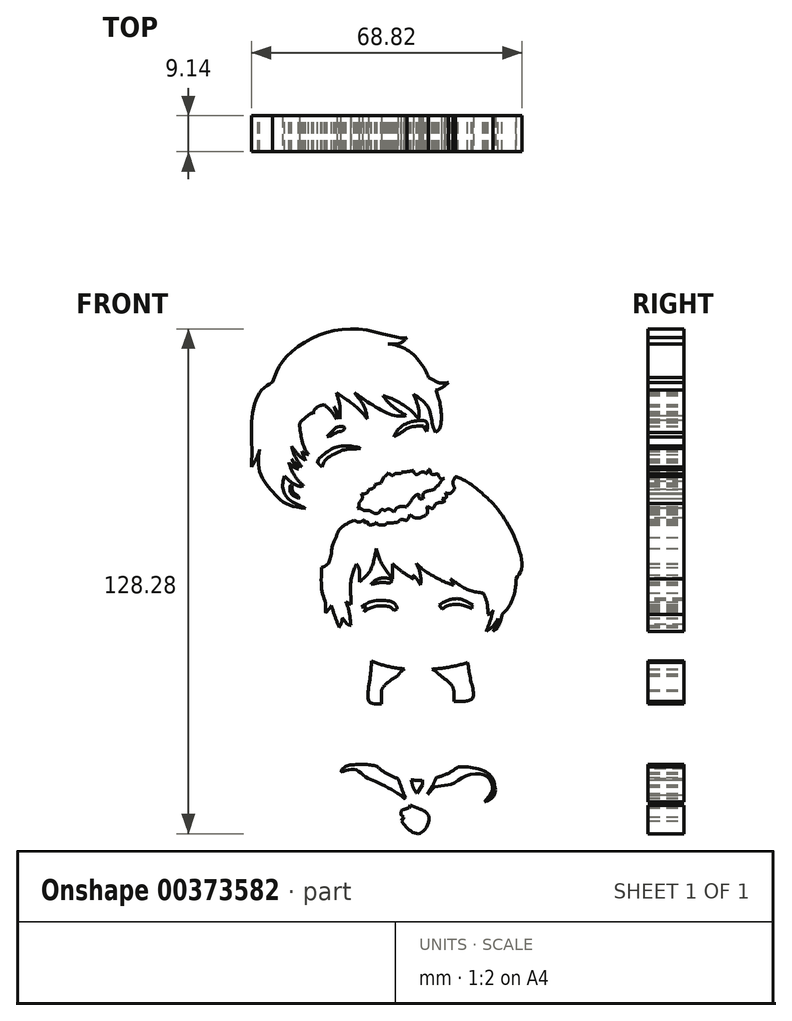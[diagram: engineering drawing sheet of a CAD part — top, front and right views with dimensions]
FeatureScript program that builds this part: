
annotation { "Feature Type Name" : "Feature", "Feature Type Description" : "" }
export const myFeature = defineFeature(function(context is Context, id is Id, definition is map)
    precondition{}
    {
        {
            var Q0;
            Q0=qCreatedBy(makeId("Front.planeOp"),FACE);
            var sketch = newSketch(context, id + "F0", { "sketchPlane" : qUnion([Q0])});
            skFitSpline(sketch, "E0", {"points": [v(-35.78, 54.46) * mm, v(-33.09, 59.85) * mm, v(-24.77, 66.06) * mm, v(-13.06, 67.81) * mm, v(-3.45, 65.7) * mm, v(-1.58, 65.82) * mm], "startDerivative": vector(10.86, 29.93) * mm, "endDerivative": vector(15.04, 3.36) * mm});
            skFitSpline(sketch, "E1", {"points": [v(-6.38, 64.18) * mm, v(-3.34, 64.3) * mm, v(-1.58, 65.82) * mm], "startDerivative": vector(6.22, -0.6) * mm, "endDerivative": vector(3.32, 3.98) * mm});
            skFitSpline(sketch, "E2", {"points": [v(-6.38, 64.18) * mm, v(-1.58, 62.66) * mm, v(2.4, 58.56) * mm, v(3.93, 55.63) * mm], "startDerivative": vector(14.2, -2.58) * mm, "endDerivative": vector(4.35, -9.84) * mm});
            skFitSpline(sketch, "E3", {"points": [v(3.93, 55.63) * mm, v(6.86, 54.23) * mm, v(8.96, 54.34) * mm], "startDerivative": vector(5.45, -3.31) * mm, "endDerivative": vector(4.6, 0.89) * mm});
            skFitSpline(sketch, "E4", {"points": [v(3.93, 54.21) * mm, v(5.68, 52.47) * mm, v(8.96, 54.34) * mm], "startDerivative": vector(3.48, -5.52) * mm, "endDerivative": vector(6.49, 5.4) * mm});
            skFitSpline(sketch, "E5", {"points": [v(5.68, 52.47) * mm, v(6.86, 48.72) * mm, v(6.86, 43.1) * mm, v(5.68, 41.7) * mm], "startDerivative": vector(3.82, -9.5) * mm, "endDerivative": vector(-5.74, -4.27) * mm});
            skFitSpline(sketch, "E6", {"points": [v(0, 51.42) * mm, v(1.35, 47.78) * mm, v(1.35, 45.1) * mm], "startDerivative": vector(3.15, -6.86) * mm, "endDerivative": vector(-0.56, -5.76) * mm});
            skFitSpline(sketch, "E7", {"points": [v(0, 51.42) * mm, v(3.93, 47.78) * mm, v(4.93, 43.33) * mm, v(5.68, 41.7) * mm], "startDerivative": vector(11.87, -7.83) * mm, "endDerivative": vector(3.7, -5.88) * mm});
            skFitSpline(sketch, "E8", {"points": [v(-7.7, 51.06) * mm, v(-5.13, 50.09) * mm, v(-0.67, 47.3) * mm, v(1.35, 45.1) * mm], "startDerivative": vector(8.03, -2.55) * mm, "endDerivative": vector(5.45, -7.1) * mm});
            skFitSpline(sketch, "E9", {"points": [v(-7.7, 51.06) * mm, v(-5.83, 48.77) * mm, v(-1.79, 45.96) * mm], "startDerivative": vector(3.67, -5.32) * mm, "endDerivative": vector(7.99, -4.9) * mm});
            skFitSpline(sketch, "E10", {"points": [v(-1.79, 45.96) * mm, v(-4.78, 45.96) * mm, v(-11.33, 49.25) * mm, v(-14.95, 51.76) * mm], "startDerivative": vector(-10.08, -1.7) * mm, "endDerivative": vector(-9.87, 7.2) * mm});
            skFitSpline(sketch, "E11", {"points": [v(-11.68, 45.1) * mm, v(-12.44, 48.14) * mm, v(-14.95, 51.76) * mm], "startDerivative": vector(-1, 6.65) * mm, "endDerivative": vector(-5.43, 6.69) * mm});
            skFitSpline(sketch, "E12", {"points": [v(-11.68, 45.1) * mm, v(-13.97, 47.7) * mm, v(-19.5, 51.76) * mm], "startDerivative": vector(-4.7, 6.12) * mm, "endDerivative": vector(-10.62, 7.16) * mm});
            skFitSpline(sketch, "E13", {"points": [v(-18.62, 45.1) * mm, v(-18.62, 48.14) * mm, v(-19.5, 51.76) * mm], "startDerivative": vector(0.4, 6.3) * mm, "endDerivative": vector(-2.13, 7.02) * mm});
            skFitSpline(sketch, "E14", {"points": [v(-20.14, 48.19) * mm, v(-19.3, 46.86) * mm, v(-18.62, 45.1) * mm], "startDerivative": vector(1.86, -2.65) * mm, "endDerivative": vector(1.2, -3.53) * mm});
            skFitSpline(sketch, "E15", {"points": [v(-22.6, 48.73) * mm, v(-20.78, 46.96) * mm, v(-19.55, 45.1) * mm], "startDerivative": vector(3.79, -3.33) * mm, "endDerivative": vector(2.3, -3.96) * mm});
            skFitSpline(sketch, "E16", {"points": [v(-20.14, 48.19) * mm, v(-19.3, 45.7) * mm, v(-19.55, 45.1) * mm], "startDerivative": vector(1.92, -4.36) * mm, "endDerivative": vector(-1.07, -1.52) * mm});
            skFitSpline(sketch, "E17", {"points": [v(-25.36, 50.22) * mm, v(-25.4, 46.4) * mm], "startDerivative": vector(-0.03, -3.81) * mm, "endDerivative": vector(-0.03, -3.81) * mm});
            skFitSpline(sketch, "E18", {"points": [v(-28.3, 48.16) * mm, v(-26.94, 47.5) * mm, v(-25.4, 46.4) * mm], "startDerivative": vector(2.87, -1.25) * mm, "endDerivative": vector(2.94, -2.24) * mm});
            skFitSpline(sketch, "E19", {"points": [v(-25.39, 47.04) * mm, v(-24.28, 48.16) * mm, v(-22.6, 48.73) * mm], "startDerivative": vector(2.06, 2.6) * mm, "endDerivative": vector(3.5, 0.8) * mm});
            skFitSpline(sketch, "E20", {"points": [v(-28.3, 48.16) * mm, v(-28.83, 43.89) * mm, v(-28.83, 43.03) * mm, v(-27.85, 38.2) * mm, v(-26.6, 36.06) * mm], "startDerivative": vector(-2.2, -17.32) * mm, "endDerivative": vector(5.7, -7.14) * mm});
            skFitSpline(sketch, "E21", {"points": [v(-28.3, 36.87) * mm, v(-27.46, 36.27) * mm, v(-26.6, 36.06) * mm], "startDerivative": vector(1.58, -1.34) * mm, "endDerivative": vector(1.82, -0.28) * mm});
            skFitSpline(sketch, "E22", {"points": [v(-30.88, 38.2) * mm, v(-29.25, 36.06) * mm, v(-27.37, 34.56) * mm], "startDerivative": vector(2.98, -4.44) * mm, "endDerivative": vector(4.04, -2.82) * mm});
            skFitSpline(sketch, "E23", {"points": [v(-28.3, 36.87) * mm, v(-27.85, 35.67) * mm, v(-27.37, 34.56) * mm], "startDerivative": vector(0.87, -2.39) * mm, "endDerivative": vector(0.98, -2.23) * mm});
            skFitSpline(sketch, "E24", {"points": [v(-30.88, 38.2) * mm, v(-30.28, 36.06) * mm, v(-28.3, 32.93) * mm], "startDerivative": vector(0.9, -4.76) * mm, "endDerivative": vector(4.12, -5.72) * mm});
            skFitSpline(sketch, "E25", {"points": [v(-30.88, 34.9) * mm, v(-29.77, 33.7) * mm, v(-28.3, 32.93) * mm], "startDerivative": vector(2.06, -2.62) * mm, "endDerivative": vector(3.1, -1.32) * mm});
            skFitSpline(sketch, "E26", {"points": [v(-30.88, 34.9) * mm, v(-30.26, 33.7) * mm, v(-29.1, 32.32) * mm], "startDerivative": vector(1.16, -2.58) * mm, "endDerivative": vector(2.37, -2.57) * mm});
            skFitSpline(sketch, "E27", {"points": [v(-31.59, 34.01) * mm, v(-30.54, 32.93) * mm, v(-29.1, 32.32) * mm], "startDerivative": vector(1.94, -2.42) * mm, "endDerivative": vector(3.02, -0.96) * mm});
            skFitSpline(sketch, "E28", {"points": [v(-31.59, 34.01) * mm, v(-30.88, 32.04) * mm, v(-29.47, 29.77) * mm, v(-27.85, 28.08) * mm], "startDerivative": vector(1.88, -6.17) * mm, "endDerivative": vector(5, -4.76) * mm});
            skFitSpline(sketch, "E29", {"points": [v(-32.7, 30.62) * mm, v(-31.27, 29.23) * mm, v(-29.1, 28.02) * mm, v(-27.85, 28.08) * mm], "startDerivative": vector(3.73, -4.02) * mm, "endDerivative": vector(4.29, 0.93) * mm});
            skFitSpline(sketch, "E30", {"points": [v(-32.7, 30.62) * mm, v(-33.17, 28.08) * mm, v(-32.15, 25.21) * mm, v(-29.1, 23.2) * mm, v(-27.37, 22.4) * mm], "startDerivative": vector(-2.96, -10.2) * mm, "endDerivative": vector(7.48, -3.45) * mm});
            skFitSpline(sketch, "E31", {"points": [v(-39.04, 37.32) * mm, v(-39.3, 32.93) * mm, v(-37.7, 28.98) * mm, v(-35.36, 26.2) * mm, v(-32.4, 23.59) * mm, v(-27.37, 22.4) * mm], "startDerivative": vector(-3.4, -21.75) * mm, "endDerivative": vector(24.84, -3.15) * mm});
            skFitSpline(sketch, "E32", {"points": [v(-39.04, 37.32) * mm, v(-39.93, 34.9) * mm, v(-41.09, 32.93) * mm], "startDerivative": vector(-1.58, -4.86) * mm, "endDerivative": vector(-2.54, -3.9) * mm});
            skFitSpline(sketch, "E33", {"points": [v(-35.78, 54.46) * mm, v(-39.04, 51.7) * mm, v(-41.02, 45.3) * mm, v(-41.02, 38.2) * mm, v(-41.09, 32.93) * mm], "startDerivative": vector(-16.55, -10.36) * mm, "endDerivative": vector(-0.72, -21.25) * mm});
            skFitSpline(sketch, "E34", {"points": [v(5.68, 41.7) * mm, v(6.42, 38.2) * mm, v(8.99, 34.9) * mm], "startDerivative": vector(0.72, -7.5) * mm, "endDerivative": vector(5.83, -6.1) * mm});
            skFitSpline(sketch, "E35", {"points": [v(8.99, 34.9) * mm, v(8.13, 34.01) * mm], "startDerivative": vector(-0.86, -0.89) * mm, "endDerivative": vector(-0.86, -0.89) * mm});
            skFitSpline(sketch, "E36", {"points": [v(-27.37, 22.4) * mm, v(-25.36, 20.57) * mm, v(-22.6, 19.8) * mm], "startDerivative": vector(3.73, -4.24) * mm, "endDerivative": vector(5.8, -0.97) * mm});
            skFitSpline(sketch, "E37", {"points": [v(-22.6, 19.8) * mm, v(-21.84, 21.8) * mm, v(-19.9, 24.77) * mm, v(-19.6, 23.8) * mm], "startDerivative": vector(1.48, 4.88) * mm, "endDerivative": vector(0.58, -6.35) * mm});
            skFitSpline(sketch, "E38", {"points": [v(-19.6, 23.8) * mm, v(-17.55, 26.1) * mm, v(-16.52, 25.98) * mm], "startDerivative": vector(3.39, 4.89) * mm, "endDerivative": vector(2.72, -1.06) * mm});
            skFitSpline(sketch, "E39", {"points": [v(-17.85, 23.8) * mm, v(-16.52, 25.98) * mm], "startDerivative": vector(1.33, 2.18) * mm, "endDerivative": vector(1.33, 2.18) * mm});
            skFitSpline(sketch, "E40", {"points": [v(-17.85, 23.8) * mm, v(-16.52, 24.3) * mm, v(-14.58, 24.3) * mm], "startDerivative": vector(2.72, 1.3) * mm, "endDerivative": vector(3.78, -0.29) * mm});
            skFitSpline(sketch, "E41", {"points": [v(-16.52, 22.4) * mm, v(-15.5, 23.24) * mm, v(-14.58, 24.3) * mm], "startDerivative": vector(2.13, 1.62) * mm, "endDerivative": vector(1.74, 2.17) * mm});
            skFitSpline(sketch, "E42", {"points": [v(-16.21, 20.46) * mm, v(-15.04, 21.35) * mm, v(-13.87, 22.8) * mm, v(-13.8, 23.8) * mm], "startDerivative": vector(3.34, 2.31) * mm, "endDerivative": vector(-0.34, 3.44) * mm});
            skFitSpline(sketch, "E43", {"points": [v(-16.52, 22.4) * mm, v(-15.73, 22.4) * mm, v(-14.58, 23.34) * mm, v(-14.38, 23.8) * mm, v(-13.8, 23.8) * mm], "startDerivative": vector(2.93, -0.64) * mm, "endDerivative": vector(3.34, -0.57) * mm});
            skFitSpline(sketch, "E44", {"points": [v(-19.6, 14.98) * mm, v(-18.89, 16.78) * mm, v(-16.52, 18.65) * mm, v(-14.58, 19.8) * mm, v(-14.58, 20.74) * mm, v(-16.21, 20.46) * mm], "startDerivative": vector(2.25, 9.04) * mm, "endDerivative": vector(-10.8, -4.04) * mm});
            skFitSpline(sketch, "E45", {"points": [v(-22.6, 19.8) * mm, v(-22.6, 18.51) * mm, v(-24.71, 14.98) * mm, v(-26.6, 12.03) * mm, v(-26.6, 10.16) * mm, v(-25.36, 7.7) * mm, v(-21.84, 8.1) * mm, v(-20.6, 12.48) * mm, v(-19.6, 14.98) * mm], "startDerivative": vector(2.63, -13.87) * mm, "endDerivative": vector(9.82, 18.02) * mm});
            skFitSpline(sketch, "E46", {"points": [v(-13.8, 37.83) * mm, v(-16.21, 38.2) * mm, v(-19.35, 38) * mm, v(-21.24, 37.1) * mm, v(-23.55, 35.39) * mm, v(-24.34, 34.01) * mm], "startDerivative": vector(-11.21, 2.22) * mm, "endDerivative": vector(-3.42, -8.47) * mm});
            skFitSpline(sketch, "E47", {"points": [v(-24.34, 34.01) * mm, v(-23.68, 33.33) * mm, v(-23.2, 32.93) * mm], "startDerivative": vector(1.23, -1.34) * mm, "endDerivative": vector(1.03, -0.8) * mm});
            skFitSpline(sketch, "E48", {"points": [v(-13.8, 37.83) * mm, v(-13.43, 37.6) * mm], "startDerivative": vector(0.37, -0.23) * mm, "endDerivative": vector(0.37, -0.23) * mm});
            skFitSpline(sketch, "E49", {"points": [v(-23.2, 32.93) * mm, v(-22.84, 33.82) * mm, v(-21.55, 35.3) * mm, v(-18.85, 36.72) * mm, v(-17.55, 37.26) * mm, v(-14.32, 37.51) * mm, v(-13.43, 37.6) * mm], "startDerivative": vector(2.32, 7) * mm, "endDerivative": vector(5.9, 0.82) * mm});
            skFitSpline(sketch, "E50", {"points": [v(-23.2, 32.93) * mm, v(-22.16, 32.07) * mm, v(-20.07, 31.13) * mm, v(-17.58, 31.02) * mm, v(-13.18, 32.93) * mm], "startDerivative": vector(5.1, -4.84) * mm, "endDerivative": vector(13.78, 7.2) * mm});
            skFitSpline(sketch, "E51", {"points": [v(-13.18, 32.93) * mm, v(-12.97, 34.38) * mm, v(-13.18, 36.06) * mm, v(-13.43, 37.05) * mm, v(-13.73, 37.56) * mm], "startDerivative": vector(1.07, 4.96) * mm, "endDerivative": vector(-1.82, 2.61) * mm});
            skFitSpline(sketch, "E52", {"points": [v(-16.59, 31.32) * mm, v(-17.53, 31.95) * mm, v(-18.37, 33.45) * mm, v(-18.45, 35.12) * mm, v(-17.58, 36.38) * mm, v(-16.01, 36.66) * mm, v(-14.94, 36.4) * mm, v(-14.2, 35.1) * mm, v(-14.22, 32.93) * mm, v(-14.33, 32.34) * mm], "startDerivative": vector(-9.83, 5) * mm, "endDerivative": vector(-1.64, -6.43) * mm});
            skFitSpline(sketch, "E53", {"points": [v(-17.58, 34.3) * mm, v(-17.55, 33.82) * mm, v(-17.21, 33.22) * mm, v(-16.8, 33.82) * mm, v(-16.46, 34.13) * mm, v(-16.42, 35.27) * mm, v(-16.8, 35.7) * mm, v(-17.55, 35.46) * mm, v(-17.79, 34.9) * mm, v(-17.75, 34.54) * mm, v(-17.58, 34.3) * mm]});
            skFitSpline(sketch, "E54", {"points": [v(-14.94, 34.22) * mm, v(-14.62, 34.17) * mm, v(-14.56, 33.22) * mm, v(-15, 33.22) * mm, v(-15.46, 33.22) * mm, v(-15.78, 33.22) * mm, v(-16, 33.45) * mm, v(-15.29, 33.53) * mm, v(-14.99, 33.82) * mm, v(-14.94, 34.22) * mm]});
            skFitSpline(sketch, "E55", {"points": [v(-21.86, 40.58) * mm, v(-20.54, 42) * mm, v(-19.37, 43) * mm, v(-17.81, 43.17) * mm, v(-17.4, 42.76) * mm, v(-17.79, 42.15) * mm, v(-19.19, 41.75) * mm, v(-20.51, 41.11) * mm, v(-21.86, 40.58) * mm]});
            skFitSpline(sketch, "E56", {"points": [v(-30.97, 28.2) * mm, v(-31.3, 28.04) * mm, v(-31.35, 27.36) * mm, v(-31.27, 26.59) * mm, v(-30.7, 25.8) * mm, v(-29.36, 25) * mm, v(-29.04, 24.94) * mm, v(-29.2, 25.39) * mm, v(-29.7, 25.86) * mm, v(-30.46, 26.52) * mm, v(-30.7, 26.9) * mm, v(-30.82, 27.76) * mm, v(-30.97, 28.2) * mm]});
            skFitSpline(sketch, "E57", {"points": [v(-28.79, 44.25) * mm, v(-27.31, 45.49) * mm, v(-25.77, 46.69) * mm], "startDerivative": vector(2.92, 2.5) * mm, "endDerivative": vector(3.1, 2.35) * mm});
            skFitSpline(sketch, "E58", {"points": [v(-23.28, 7.38) * mm, v(-23.34, 3.18) * mm, v(-22.86, 0) * mm, v(-22.26, -2.26) * mm, v(-22.26, -4.08) * mm, v(-21.65, -3.47) * mm, v(-20.8, -2.26) * mm], "startDerivative": vector(-0.82, -18.5) * mm, "endDerivative": vector(5.85, 8.57) * mm});
            skFitSpline(sketch, "E59", {"points": [v(-20.8, -2.26) * mm, v(-19.94, -4.93) * mm, v(-18.82, -7.88) * mm], "startDerivative": vector(1.69, -5.44) * mm, "endDerivative": vector(2.28, -5.8) * mm});
            skFitSpline(sketch, "E60", {"points": [v(-18.82, -7.88) * mm, v(-18.2, -6.6) * mm, v(-18, -5.44) * mm], "startDerivative": vector(1.37, 2.44) * mm, "endDerivative": vector(0.25, 2.45) * mm});
            skFitSpline(sketch, "E61", {"points": [v(-18, -5.44) * mm, v(-16.63, -7.12) * mm, v(-15.87, -7.32) * mm], "startDerivative": vector(2.26, -3.36) * mm, "endDerivative": vector(2, -0.14) * mm});
            skFitSpline(sketch, "E62", {"points": [v(-17.14, -1.42) * mm, v(-16.38, -3.5) * mm, v(-15.87, -7.32) * mm], "startDerivative": vector(1.96, -4.43) * mm, "endDerivative": vector(0.65, -7.25) * mm});
            skFitSpline(sketch, "E63", {"points": [v(-17.14, -1.42) * mm, v(-15.87, -2.06) * mm], "startDerivative": vector(1.27, -0.64) * mm, "endDerivative": vector(1.27, -0.64) * mm});
            skFitSpline(sketch, "E64", {"points": [v(-14.4, 8.3) * mm, v(-15.2, 6.36) * mm, v(-15.87, 3.77) * mm, v(-15.87, 0) * mm, v(-15.87, -2.06) * mm], "startDerivative": vector(-3.72, -8.42) * mm, "endDerivative": vector(-0.16, -8.38) * mm});
            skFitSpline(sketch, "E65", {"points": [v(-14.4, 8.3) * mm, v(-13.73, 6.87) * mm, v(-13.68, 3.62) * mm], "startDerivative": vector(1.93, -3.06) * mm, "endDerivative": vector(-0.36, -6.12) * mm});
            skFitSpline(sketch, "E66", {"points": [v(-9.36, 12.16) * mm, v(-9.97, 9.37) * mm, v(-11.09, 6.36) * mm, v(-13.68, 3.62) * mm], "startDerivative": vector(-1.82, -8.85) * mm, "endDerivative": vector(-8.2, -7.26) * mm});
            skFitSpline(sketch, "E67", {"points": [v(-9.36, 12.16) * mm, v(-8.44, 9.15) * mm, v(-6.35, 5.84) * mm, v(-5.23, 4.47) * mm], "startDerivative": vector(1.84, -8.43) * mm, "endDerivative": vector(3.88, -4.54) * mm});
            skFitSpline(sketch, "E68", {"points": [v(-5.23, 8.3) * mm, v(-5.23, 4.47) * mm], "startDerivative": vector(0, -3.83) * mm, "endDerivative": vector(0, -3.83) * mm});
            skFitSpline(sketch, "E69", {"points": [v(-5.23, 8.3) * mm, v(-2.64, 6.14) * mm, v(0, 4.47) * mm], "startDerivative": vector(5.02, -4.43) * mm, "endDerivative": vector(5.45, -3.23) * mm});
            skFitSpline(sketch, "E70", {"points": [v(-0.65, 6.2) * mm, v(0, 5.43) * mm, v(0, 4.47) * mm], "startDerivative": vector(1.62, -1.4) * mm, "endDerivative": vector(-0.32, -2.06) * mm});
            skFitSpline(sketch, "E71", {"points": [v(0, 5.43) * mm, v(0.87, 4.47) * mm, v(1.84, 2.89) * mm], "startDerivative": vector(1.94, -1.94) * mm, "endDerivative": vector(1.74, -3.11) * mm});
            skFitSpline(sketch, "E72", {"points": [v(0.77, 8.38) * mm, v(1.53, 6.6) * mm, v(1.94, 4.47) * mm, v(1.84, 2.89) * mm], "startDerivative": vector(2.45, -5.04) * mm, "endDerivative": vector(-0.63, -4.93) * mm});
            skFitSpline(sketch, "E73", {"points": [v(0.77, 8.38) * mm, v(3.16, 6.35) * mm, v(8.35, 3.5) * mm, v(10.23, 2.89) * mm], "startDerivative": vector(6.23, -6.11) * mm, "endDerivative": vector(6.35, -1.6) * mm});
            skFitSpline(sketch, "E74", {"points": [v(8.4, 5.43) * mm, v(9.47, 4.47) * mm, v(10.23, 2.89) * mm], "startDerivative": vector(2.43, -1.8) * mm, "endDerivative": vector(1.25, -3.26) * mm});
            skFitSpline(sketch, "E75", {"points": [v(9.47, 4.47) * mm, v(11.3, 3.17) * mm, v(14.43, 1.5) * mm, v(17.76, 0.9) * mm], "startDerivative": vector(5.9, -4.32) * mm, "endDerivative": vector(9.5, -0.91) * mm});
            skFitSpline(sketch, "E76", {"points": [v(17.76, 0.9) * mm, v(18.62, -1.15) * mm, v(18.96, -4.2) * mm, v(18.83, -4.8) * mm], "startDerivative": vector(2.57, -4.83) * mm, "endDerivative": vector(-0.84, -2.34) * mm});
            skFitSpline(sketch, "E77", {"points": [v(20.29, -1.88) * mm, v(20.25, -3.6) * mm, v(18.89, -4.64) * mm], "startDerivative": vector(0.57, -3.76) * mm, "endDerivative": vector(-3.37, -1.76) * mm});
            skFitSpline(sketch, "E78", {"points": [v(20.25, -3.6) * mm, v(19.66, -5.87) * mm, v(18.54, -8.86) * mm], "startDerivative": vector(-1.1, -4.78) * mm, "endDerivative": vector(-2.28, -5.73) * mm});
            skFitSpline(sketch, "E79", {"points": [v(18.54, -8.86) * mm, v(20.25, -7.54) * mm, v(21.54, -5.65) * mm], "startDerivative": vector(3.67, 2.44) * mm, "endDerivative": vector(2.32, 3.97) * mm});
            skFitSpline(sketch, "E80", {"points": [v(20.25, -8.86) * mm, v(21.11, -7.37) * mm, v(21.54, -5.65) * mm], "startDerivative": vector(1.96, 2.91) * mm, "endDerivative": vector(0.63, 3.5) * mm});
            skFitSpline(sketch, "E81", {"points": [v(20.25, -8.86) * mm, v(21.54, -7.7) * mm, v(22.57, -4.64) * mm], "startDerivative": vector(3.33, 2.19) * mm, "endDerivative": vector(1.4, 6.06) * mm});
            skFitSpline(sketch, "E82", {"points": [v(26.04, 4.47) * mm, v(25.9, 1.67) * mm, v(24.3, -2.57) * mm, v(22.57, -4.64) * mm], "startDerivative": vector(0.27, -8.4) * mm, "endDerivative": vector(-5.95, -5.77) * mm});
            skFitSpline(sketch, "E83", {"points": [v(20.25, 23.62) * mm, v(23.8, 18.8) * mm, v(26.54, 12.9) * mm, v(27.62, 7.28) * mm, v(26.04, 4.47) * mm], "startDerivative": vector(14.13, -17.43) * mm, "endDerivative": vector(-10.63, -12.77) * mm});
            skFitSpline(sketch, "E84", {"points": [v(10.72, 30.44) * mm, v(14.03, 28.92) * mm, v(20.25, 23.62) * mm], "startDerivative": vector(7.85, -2.76) * mm, "endDerivative": vector(10.99, -10.37) * mm});
            skFitSpline(sketch, "E85", {"points": [v(-18.43, -7.16) * mm, v(-17.63, -8.03) * mm, v(-16.42, -9) * mm], "startDerivative": vector(1.6, -1.88) * mm, "endDerivative": vector(2.41, -1.8) * mm});
            skFitSpline(sketch, "E86", {"points": [v(-16.42, -9) * mm, v(-16.15, -11.08) * mm, v(-15.76, -12.96) * mm, v(-14.27, -14.41) * mm], "startDerivative": vector(0.9, -6.15) * mm, "endDerivative": vector(5.24, -3.93) * mm});
            skFitSpline(sketch, "E87", {"points": [v(-14.27, -14.41) * mm, v(-8.74, -17.13) * mm, v(0.52, -18.6) * mm, v(10.03, -17.8) * mm, v(16.3, -15.35) * mm, v(18.33, -11.69) * mm, v(18.99, -9.75) * mm, v(20.25, -8.86) * mm], "startDerivative": vector(32.62, -19.16) * mm, "endDerivative": vector(18.52, 9.45) * mm});
            skFitSpline(sketch, "E88", {"points": [v(-4.09, -11.59) * mm, v(-3.93, -13.01) * mm, v(-1.75, -14.74) * mm, v(3.5, -14.95) * mm, v(6.4, -13.78) * mm, v(7.16, -12.5) * mm], "startDerivative": vector(-0.66, -9.66) * mm, "endDerivative": vector(3.65, 8.99) * mm});
            skFitSpline(sketch, "E89", {"points": [v(-4.09, -11.59) * mm, v(-1.75, -11.18) * mm, v(2.88, -11.13) * mm, v(6.34, -11.59) * mm, v(7.16, -12.5) * mm], "startDerivative": vector(9.19, 2.09) * mm, "endDerivative": vector(3.56, -6.23) * mm});
            skFitSpline(sketch, "E90", {"points": [v(-13.14, -2.74) * mm, v(-11.16, -1.46) * mm, v(-7.19, -1) * mm, v(-4.7, -1.87) * mm, v(-4.09, -3.2) * mm], "startDerivative": vector(7.11, 5.91) * mm, "endDerivative": vector(1.95, -7.59) * mm});
            skFitSpline(sketch, "E91", {"points": [v(-12.53, -3.9) * mm, v(-10.3, -2.69) * mm, v(-6.22, -2.58) * mm, v(-4.9, -3.6) * mm], "startDerivative": vector(5.8, 4.3) * mm, "endDerivative": vector(3.8, -4.53) * mm});
            skLineSegment(sketch, "E92", {"start": v(-13.14, -2.74) * mm, "end": v(-11.9, -2.74) * mm});
            skLineSegment(sketch, "E93", {"start": v(-11.9, -2.74) * mm, "end": v(-12.53, -3.9) * mm});
            skLineSegment(sketch, "E94", {"start": v(-4.9, -3.6) * mm, "end": v(-4.09, -3.2) * mm});
            skLineSegment(sketch, "E95", {"start": v(6.55, -2.23) * mm, "end": v(7.31, -3.2) * mm});
            skFitSpline(sketch, "E96", {"points": [v(6.55, -2.23) * mm, v(8.38, -1.16) * mm, v(9.6, -0.75) * mm, v(11.79, -0.65) * mm, v(15.15, -2.23) * mm], "startDerivative": vector(8, 5.03) * mm, "endDerivative": vector(10.7, -6.4) * mm});
            skFitSpline(sketch, "E97", {"points": [v(7.31, -3.2) * mm, v(8.74, -2.4) * mm, v(11.46, -2.07) * mm, v(14.47, -2.85) * mm, v(14.97, -3.2) * mm], "startDerivative": vector(5.6, 3.74) * mm, "endDerivative": vector(2.6, -2.24) * mm});
            skLineSegment(sketch, "E98", {"start": v(14.97, -3.2) * mm, "end": v(14.75, -2.5) * mm});
            skLineSegment(sketch, "E99", {"start": v(14.75, -2.5) * mm, "end": v(15.15, -2.23) * mm});
            skFitSpline(sketch, "E100", {"points": [v(-10.76, 3.1) * mm, v(-9.28, 4.27) * mm, v(-7.37, 4.73) * mm, v(-5.92, 4.45) * mm], "startDerivative": vector(3.94, 3.8) * mm, "endDerivative": vector(4.52, -1.34) * mm});
            skFitSpline(sketch, "E101", {"points": [v(-10.76, 3.1) * mm, v(-9.5, 3.3) * mm, v(-7.58, 3.56) * mm, v(-5.72, 3.53) * mm, v(-5.46, 4.12) * mm, v(-5.92, 4.45) * mm], "startDerivative": vector(5.75, 0.81) * mm, "endDerivative": vector(-4.31, 1.76) * mm});
            skFitSpline(sketch, "E102", {"points": [v(0.85, -8.55) * mm, v(1.9, -8.23) * mm, v(2.45, -7.68) * mm, v(2.9, -7.71) * mm, v(2.7, -8.55) * mm, v(0.85, -8.55) * mm]});
            skFitSpline(sketch, "E103", {"points": [v(-2.2, -18.44) * mm, v(-1.78, -19.48) * mm, v(0, -20.69) * mm, v(0.97, -21.23) * mm, v(1, -21.96) * mm, v(1.06, -23.14) * mm, v(1.3, -23.65) * mm], "startDerivative": vector(1.27, -6.3) * mm, "endDerivative": vector(2.3, -3.66) * mm});
            skFitSpline(sketch, "E104", {"points": [v(4.57, -18.5) * mm, v(4.57, -19.45) * mm, v(4.03, -20.42) * mm, v(2.27, -20.72) * mm, v(2.03, -21.63) * mm, v(2.03, -22.14) * mm, v(1.58, -22.93) * mm, v(1.3, -23.65) * mm], "startDerivative": vector(0.44, -6.45) * mm, "endDerivative": vector(-1.58, -5.57) * mm});
            skFitSpline(sketch, "E105", {"points": [v(2.05, -21.8) * mm, v(3.03, -22.55) * mm, v(4.74, -24.36) * mm], "startDerivative": vector(2.26, -1.57) * mm, "endDerivative": vector(3.07, -3.46) * mm});
            skFitSpline(sketch, "E106", {"points": [v(4.74, -24.36) * mm, v(5.52, -22.62) * mm, v(5.96, -21.76) * mm, v(6.3, -20.28) * mm, v(6.42, -19.7) * mm], "startDerivative": vector(2.6, 6.16) * mm, "endDerivative": vector(0.63, 2.75) * mm});
            skFitSpline(sketch, "E107", {"points": [v(4.74, -18.5) * mm, v(5.46, -18.87) * mm, v(6.42, -19.7) * mm], "startDerivative": vector(1.6, -0.7) * mm, "endDerivative": vector(1.74, -1.68) * mm});
            skFitSpline(sketch, "E108", {"points": [v(-1.58, -24.52) * mm, v(-0.83, -23.1) * mm, v(0, -22.03) * mm], "startDerivative": vector(1.38, 2.82) * mm, "endDerivative": vector(1.8, 2.13) * mm});
            skFitSpline(sketch, "E109", {"points": [v(0, -22.03) * mm, v(0.3, -22.55) * mm, v(0.87, -23.26) * mm, v(1.15, -23.38) * mm], "startDerivative": vector(0.72, -1.4) * mm, "endDerivative": vector(1.1, -0.25) * mm});
            skFitSpline(sketch, "E110", {"points": [v(1.43, -23.25) * mm, v(2.06, -23.12) * mm, v(2.38, -22.67) * mm, v(2.38, -22.47) * mm, v(2.6, -22.19) * mm], "startDerivative": vector(2.17, 0.05) * mm, "endDerivative": vector(1.29, 1.29) * mm});
            skFitSpline(sketch, "E111", {"points": [v(-4.86, 40.56) * mm, v(-3.95, 42.26) * mm, v(-0.8, 44.32) * mm, v(3.03, 44.62) * mm], "startDerivative": vector(2.4, 6.38) * mm, "endDerivative": vector(10.4, -0.42) * mm});
            skFitSpline(sketch, "E112", {"points": [v(-4.86, 40.56) * mm, v(-3.1, 41.6) * mm, v(-1.1, 42.86) * mm, v(2.6, 43.35) * mm], "startDerivative": vector(6.11, 3.24) * mm, "endDerivative": vector(10.26, 0.35) * mm});
            skFitSpline(sketch, "E113", {"points": [v(3.03, 44.62) * mm, v(3.5, 44.07) * mm, v(3.5, 41.9) * mm], "startDerivative": vector(1.5, -1.14) * mm, "endDerivative": vector(-0.4, -4.04) * mm});
            skFitSpline(sketch, "E114", {"points": [v(2.6, 43.35) * mm, v(3.5, 41.9) * mm], "startDerivative": vector(0.9, -1.45) * mm, "endDerivative": vector(0.9, -1.45) * mm});
            skFitSpline(sketch, "E115", {"points": [v(3.5, 41.9) * mm, v(3.5, 40.56) * mm, v(3.03, 39.25) * mm, v(1.35, 38.03) * mm, v(-1.32, 36.41) * mm], "startDerivative": vector(0.33, -6.36) * mm, "endDerivative": vector(-8.61, -5.3) * mm});
            skFitSpline(sketch, "E116", {"points": [v(-4.58, 40.71) * mm, v(-4.26, 39.7) * mm, v(-2.91, 37.42) * mm, v(-1.32, 36.41) * mm], "startDerivative": vector(0.9, -3.44) * mm, "endDerivative": vector(4.86, -2.15) * mm});
            skFitSpline(sketch, "E117", {"points": [v(1.21, 37.95) * mm, v(1.21, 38.84) * mm, v(1.06, 40.14) * mm, v(-0.32, 41.9) * mm, v(-2.2, 41.61) * mm, v(-3.11, 40.35) * mm, v(-2.88, 38.79) * mm, v(-2, 37.6) * mm, v(-0.65, 36.82) * mm], "startDerivative": vector(-0.04, 9.15) * mm, "endDerivative": vector(11.42, -5.53) * mm});
            skFitSpline(sketch, "E118", {"points": [v(-2.1, 40.9) * mm, v(-2.5, 40.56) * mm, v(-2.48, 39.94) * mm, v(-2.23, 39.74) * mm, v(-2.03, 39) * mm, v(-1.89, 38.6) * mm, v(-1.7, 38.86) * mm, v(-1.57, 39.3) * mm, v(-1.32, 39.31) * mm, v(-1.08, 39.92) * mm, v(-1.32, 40.88) * mm, v(-2.1, 40.9) * mm]});
            skFitSpline(sketch, "E119", {"points": [v(0.34, 39.56) * mm, v(0, 39.11) * mm, v(0.23, 38.86) * mm, v(0.38, 38.45) * mm, v(0.63, 38.54) * mm, v(0.74, 39.13) * mm, v(0.34, 39.56) * mm]});
            skFitSpline(sketch, "E120", {"points": [v(-2.2, -18.44) * mm, v(-3.13, -19.15) * mm, v(-3.83, -20.06) * mm, v(-3.9, -20.48) * mm], "startDerivative": vector(-2.44, -1.65) * mm, "endDerivative": vector(0.03, -1.67) * mm});
            skFitSpline(sketch, "E121", {"points": [v(-3.9, -20.48) * mm, v(-3.2, -21.57) * mm, v(-2.56, -22.72) * mm, v(-1.58, -24.52) * mm], "startDerivative": vector(2.36, -3.57) * mm, "endDerivative": vector(2.69, -4.92) * mm});
            skFitSpline(sketch, "E122", {"points": [v(-3.88, -20.21) * mm, v(-4.72, -20.6) * mm, v(-7.43, -22.8) * mm, v(-8, -23.82) * mm], "startDerivative": vector(-2.78, -0.96) * mm, "endDerivative": vector(-1.18, -3.3) * mm});
            skFitSpline(sketch, "E123", {"points": [v(-8, -23.82) * mm, v(-8, -27.3) * mm, v(-8, -29.13) * mm, v(-8.42, -31.26) * mm], "startDerivative": vector(-0.1, -9.5) * mm, "endDerivative": vector(-1.7, -7.06) * mm});
            skFitSpline(sketch, "E124", {"points": [v(-8.42, -31.26) * mm, v(-6.64, -32.13) * mm, v(-3.28, -31.87) * mm, v(-2.13, -31.77) * mm], "startDerivative": vector(4.64, -3.44) * mm, "endDerivative": vector(3.81, 0.18) * mm});
            skFitSpline(sketch, "E125", {"points": [v(3.74, -30.6) * mm, v(4.9, -31.26) * mm, v(8.78, -31.67) * mm, v(10.5, -31.26) * mm], "startDerivative": vector(3.44, -2.62) * mm, "endDerivative": vector(4.84, 1.76) * mm});
            skFitSpline(sketch, "E126", {"points": [v(6.42, -19.7) * mm, v(7.8, -20.79) * mm, v(9.74, -22.54) * mm, v(10.32, -23.97) * mm], "startDerivative": vector(3.98, -3.17) * mm, "endDerivative": vector(1.17, -4.82) * mm});
            skFitSpline(sketch, "E127", {"points": [v(10.32, -23.97) * mm, v(10.32, -26.7) * mm, v(10.32, -29.67) * mm, v(10.5, -31.26) * mm], "startDerivative": vector(0.05, -7.4) * mm, "endDerivative": vector(0.84, -5.33) * mm});
            skFitSpline(sketch, "E128", {"points": [v(13.83, -16.79) * mm, v(14.7, -21.7) * mm, v(15.07, -25.82) * mm, v(12.53, -26.67) * mm, v(10.32, -26.7) * mm], "startDerivative": vector(2.3, -15.84) * mm, "endDerivative": vector(-10.1, 0.17) * mm});
            skFitSpline(sketch, "E129", {"points": [v(-10.6, -16.4) * mm, v(-11.07, -21.47) * mm, v(-11.2, -26.7) * mm, v(-8, -27.3) * mm], "startDerivative": vector(-0.77, -13.29) * mm, "endDerivative": vector(13.92, 0.84) * mm});
            skFitSpline(sketch, "E130", {"points": [v(-2.13, -31.77) * mm, v(-2.13, -36.55) * mm, v(-0.86, -44.6) * mm, v(0, -48.5) * mm, v(0.96, -50.07) * mm], "startDerivative": vector(-0.95, -16.69) * mm, "endDerivative": vector(6.48, -8.72) * mm});
            skFitSpline(sketch, "E131", {"points": [v(-7.28, -31.96) * mm, v(-7.23, -34.16) * mm, v(-5.3, -41.85) * mm, v(-2.33, -50.5) * mm], "startDerivative": vector(-0.57, -9.22) * mm, "endDerivative": vector(7.34, -20.39) * mm});
            skFitSpline(sketch, "E132", {"points": [v(9.52, -31.56) * mm, v(8.57, -35.71) * mm, v(7.04, -42.63) * mm, v(4.9, -48.23) * mm], "startDerivative": vector(-3.26, -13.28) * mm, "endDerivative": vector(-6.75, -15.51) * mm});
            skFitSpline(sketch, "E133", {"points": [v(4.04, -30.83) * mm, v(4.04, -31.64) * mm, v(3.31, -37.55) * mm, v(2.3, -47.93) * mm], "startDerivative": vector(0.28, -4.57) * mm, "endDerivative": vector(-1.89, -21.56) * mm});
            skFitSpline(sketch, "E134", {"points": [v(13.72, -26.54) * mm, v(13.67, -29.99) * mm, v(13.73, -35.38) * mm, v(13.92, -40.15) * mm], "startDerivative": vector(-0.25, -11.06) * mm, "endDerivative": vector(0.61, -13.46) * mm});
            skFitSpline(sketch, "E135", {"points": [v(9.34, -32.31) * mm, v(9.82, -36.87) * mm, v(10.13, -40.15) * mm, v(10.13, -41.58) * mm, v(10.88, -42.2) * mm, v(11.37, -43.38) * mm], "startDerivative": vector(1.4, -15.85) * mm, "endDerivative": vector(2.14, -8.64) * mm});
            skFitSpline(sketch, "E136", {"points": [v(-7.32, -33.12) * mm, v(-7.71, -36.2) * mm, v(-7.71, -37.77) * mm, v(-7.8, -39.1) * mm, v(-8, -39.76) * mm, v(-8, -40.9) * mm, v(-8.49, -41.8) * mm, v(-9, -42.11) * mm, v(-9.21, -43.15) * mm], "startDerivative": vector(-2.64, -16.89) * mm, "endDerivative": vector(-0.53, -10.83) * mm});
            skFitSpline(sketch, "E137", {"points": [v(-9.21, -43.15) * mm, v(-7.79, -44.39) * mm, v(-5.55, -45.6) * mm, v(-3.81, -46.34) * mm], "startDerivative": vector(4.1, -4.02) * mm, "endDerivative": vector(5.4, -2.04) * mm});
            skFitSpline(sketch, "E138", {"points": [v(-0.5, -46.61) * mm, v(0.88, -46.72) * mm, v(2.4, -46.68) * mm], "startDerivative": vector(2.8, -0.29) * mm, "endDerivative": vector(3.04, 0.15) * mm});
            skFitSpline(sketch, "E139", {"points": [v(5.86, -46) * mm, v(8.42, -45.18) * mm, v(11.37, -43.38) * mm], "startDerivative": vector(5.45, 1.34) * mm, "endDerivative": vector(5.58, 3.83) * mm});
            skFitSpline(sketch, "E140", {"points": [v(13.92, -40.15) * mm, v(10.13, -40.15) * mm], "startDerivative": vector(-3.78, 0) * mm, "endDerivative": vector(-3.78, 0) * mm});
            skFitSpline(sketch, "E141", {"points": [v(13.92, -43.38) * mm, v(13.92, -40.15) * mm], "startDerivative": vector(0, 3.22) * mm, "endDerivative": vector(0, 3.22) * mm});
            skFitSpline(sketch, "E142", {"points": [v(11.37, -43.38) * mm, v(13.92, -43.38) * mm, v(18.25, -44.44) * mm, v(20.2, -46.46) * mm, v(20.62, -50.35) * mm, v(17, -52.54) * mm, v(10.75, -53.8) * mm, v(7.9, -54.12) * mm, v(4.9, -54.42) * mm], "startDerivative": vector(22.04, 1.3) * mm, "endDerivative": vector(-27.53, -2.77) * mm});
            skFitSpline(sketch, "E143", {"points": [v(4.9, -48.23) * mm, v(3.6, -50.27) * mm], "startDerivative": vector(-1.3, -2.05) * mm, "endDerivative": vector(-1.3, -2.05) * mm});
            skFitSpline(sketch, "E144", {"points": [v(2.3, -47.93) * mm, v(0.96, -50.07) * mm], "startDerivative": vector(-1.34, -2.14) * mm, "endDerivative": vector(-1.34, -2.14) * mm});
            skFitSpline(sketch, "E145", {"points": [v(3.6, -50.27) * mm, v(5.42, -48.46) * mm], "startDerivative": vector(1.82, 1.82) * mm, "endDerivative": vector(1.82, 1.82) * mm});
            skFitSpline(sketch, "E146", {"points": [v(5.42, -48.46) * mm, v(7.7, -48.06) * mm, v(10, -47.59) * mm, v(13.36, -45.61) * mm, v(17.63, -45.22) * mm, v(19.64, -46.8) * mm, v(20.03, -49.6) * mm, v(19.2, -50.87) * mm, v(18.09, -52.2) * mm], "startDerivative": vector(19.5, 3.85) * mm, "endDerivative": vector(-11.06, -13.53) * mm});
            skFitSpline(sketch, "E147", {"points": [v(-9.21, -43.15) * mm, v(-11.52, -42.73) * mm, v(-14.56, -42.73) * mm, v(-17.14, -43.15) * mm, v(-18.5, -44.68) * mm], "startDerivative": vector(-9.17, 2.14) * mm, "endDerivative": vector(-5.04, -8) * mm});
            skFitSpline(sketch, "E148", {"points": [v(-3.13, -50.5) * mm, v(-6.67, -48.46) * mm, v(-9.87, -46.86) * mm, v(-11.89, -45.97) * mm, v(-13.9, -44.42) * mm, v(-15.65, -43.9) * mm, v(-17.8, -44.42) * mm, v(-18.5, -44.68) * mm, v(-18.89, -45.97) * mm, v(-18.95, -47.93) * mm, v(-17.4, -50.27) * mm, v(-13.57, -52.11) * mm, v(-8.32, -54.33) * mm, v(-7.3, -54.89) * mm, v(-6.3, -55.22) * mm], "startDerivative": vector(-37.34, 22.1) * mm, "endDerivative": vector(22.17, -6.3) * mm});
            skFitSpline(sketch, "E149", {"points": [v(-3.13, -50.5) * mm, v(-4.12, -52.41) * mm, v(-6.3, -55.22) * mm], "startDerivative": vector(-1.91, -4.23) * mm, "endDerivative": vector(-4.33, -5.17) * mm});
            skFitSpline(sketch, "E150", {"points": [v(3.6, -50.27) * mm, v(4.4, -51.39) * mm, v(4.7, -53.63) * mm, v(4.3, -54.72) * mm, v(4.9, -54.42) * mm], "startDerivative": vector(3.34, -3.74) * mm, "endDerivative": vector(4.67, 2.99) * mm});
            skFitSpline(sketch, "E151", {"points": [v(-3.13, -50.5) * mm, v(-1.75, -51.98) * mm, v(-0.66, -53.04) * mm], "startDerivative": vector(2.65, -2.9) * mm, "endDerivative": vector(2.3, -2.17) * mm});
            skPoint(sketch, "E152.1.internal.snap0", {"position": v(-2.98, -64.76) * mm});
            skFitSpline(sketch, "E152", {"points": [v(-6.3, -55.22) * mm, v(-2.98, -57.07) * mm], "startDerivative": vector(3.32, -1.86) * mm, "endDerivative": vector(3.32, -1.86) * mm});
            skFitSpline(sketch, "E153", {"points": [v(-2.98, -57.07) * mm, v(-2.33, -56.05) * mm], "startDerivative": vector(0.65, 1.03) * mm, "endDerivative": vector(0.65, 1.03) * mm});
            skFitSpline(sketch, "E154", {"points": [v(-0.66, -53.04) * mm, v(-1.04, -53.75) * mm], "startDerivative": vector(-0.38, -0.7) * mm, "endDerivative": vector(-0.38, -0.7) * mm});
            skFitSpline(sketch, "E155", {"points": [v(-2.33, -56.05) * mm, v(-2.98, -55.66) * mm, v(-3.13, -54.89) * mm, v(-2.73, -54.25) * mm, v(-1.64, -53.92) * mm, v(-1.04, -53.75) * mm], "startDerivative": vector(-3.88, 1.48) * mm, "endDerivative": vector(3, 0.98) * mm});
            skFitSpline(sketch, "E156", {"points": [v(-2.33, -51.37) * mm, v(-0.44, -50.5) * mm, v(2.5, -50.27) * mm, v(3.6, -50.27) * mm], "startDerivative": vector(4.88, 2.98) * mm, "endDerivative": vector(3.74, 0) * mm});
            skFitSpline(sketch, "E157", {"points": [v(0.96, -50.07) * mm, v(0.96, -50.31) * mm], "startDerivative": vector(0, -0.24) * mm, "endDerivative": vector(0, -0.24) * mm});
            skFitSpline(sketch, "E158", {"points": [v(-0.66, -53.04) * mm, v(0.96, -53.75) * mm, v(3.6, -55.22) * mm, v(3.6, -58.14) * mm, v(1.76, -60.17) * mm, v(0, -60) * mm, v(-1.87, -58.44) * mm, v(-2.98, -57.07) * mm], "startDerivative": vector(11.36, -5.5) * mm, "endDerivative": vector(-8.07, 10.6) * mm});
            skFitSpline(sketch, "E159", {"points": [v(4.3, -54.72) * mm, v(3.1, -54.72) * mm], "startDerivative": vector(-1.2, 0) * mm, "endDerivative": vector(-1.2, 0) * mm});
            skFitSpline(sketch, "E160", {"points": [v(-9.87, -27.31) * mm, v(-9.64, -30.06) * mm, v(-9.32, -35.11) * mm, v(-9.2, -39.1) * mm, v(-9.2, -40.86) * mm, v(-8.78, -41.96) * mm], "startDerivative": vector(1.1, -12.59) * mm, "endDerivative": vector(3.94, -8.02) * mm});
            skFitSpline(sketch, "E161", {"points": [v(-9.21, -39.6) * mm, v(-8, -39.76) * mm], "startDerivative": vector(1.21, -0.17) * mm, "endDerivative": vector(1.21, -0.17) * mm});
            skFitSpline(sketch, "E162", {"points": [v(-6.76, 19.07) * mm, v(-7.3, 18.18) * mm, v(-9.2, 18.38) * mm, v(-9.32, 18.88) * mm, v(-9.87, 20.62) * mm, v(-8.78, 21.27) * mm, v(-8, 22.07) * mm, v(-7.3, 21.72) * mm, v(-7.3, 20.72) * mm, v(-6.76, 19.07) * mm]});
            skFitSpline(sketch, "E163", {"points": [v(-7.3, 21.72) * mm, v(-6.3, 22.22) * mm, v(-5.23, 21.72) * mm, v(-4.52, 20.67) * mm, v(-5.23, 19.52) * mm, v(-4.67, 18.88) * mm, v(-6.8, 18.65) * mm], "startDerivative": vector(6.38, 4.7) * mm, "endDerivative": vector(-15.2, -0.03) * mm});
            skFitSpline(sketch, "E164", {"points": [v(-4.9, 21.44) * mm, v(-3.87, 22.67) * mm, v(-2.33, 22.82) * mm, v(-1.04, 22.37) * mm, v(-1.04, 20.37) * mm, v(-1.75, 19.32) * mm, v(-2.98, 19.57) * mm, v(-3.97, 18.83) * mm, v(-4.67, 18.88) * mm], "startDerivative": vector(6.56, 10.96) * mm, "endDerivative": vector(-7.83, 2.8) * mm});
            skFitSpline(sketch, "E165", {"points": [v(-0.94, 20.8) * mm, v(0.96, 19.87) * mm, v(2.6, 20.37) * mm, v(3.6, 21.32) * mm, v(3.6, 22.87) * mm, v(4.3, 23.22) * mm, v(3.6, 24.62) * mm, v(2.6, 24.87) * mm, v(1.52, 24.91) * mm, v(1.52, 25.76) * mm, v(0.52, 25.66) * mm, v(-0.66, 24.07) * mm, v(-1.75, 22.75) * mm], "startDerivative": vector(18.42, -12.7) * mm, "endDerivative": vector(-12.24, -12.87) * mm});
            skFitSpline(sketch, "E166", {"points": [v(-9.32, 18.88) * mm, v(-9.95, 18.33) * mm, v(-11.52, 18.38) * mm, v(-11.52, 18.88) * mm, v(-12.45, 18.88) * mm, v(-12.3, 20.37) * mm, v(-12.45, 21.72) * mm, v(-11, 21.72) * mm, v(-9.95, 21.17) * mm, v(-9.32, 21.02) * mm], "startDerivative": vector(-4.1, -6.34) * mm, "endDerivative": vector(7.28, -1) * mm});
            skFitSpline(sketch, "E167", {"points": [v(-12.45, 19.54) * mm, v(-13.75, 18.88) * mm, v(-15, 19.39) * mm], "startDerivative": vector(-2.55, -1.92) * mm, "endDerivative": vector(-2.56, 1.63) * mm});
            skFitSpline(sketch, "E168", {"points": [v(-12.45, 21.72) * mm, v(-13.45, 22.37) * mm, v(-14.1, 22.37) * mm], "startDerivative": vector(-1.8, 1.46) * mm, "endDerivative": vector(-1.5, -0.24) * mm});
            skFitSpline(sketch, "E169", {"points": [v(3.6, 22.87) * mm, v(4.9, 22.37) * mm, v(5.95, 23.62) * mm, v(7.9, 24.12) * mm, v(6.86, 25.41) * mm, v(6.61, 26.41) * mm, v(5.42, 27.11) * mm, v(4.3, 26.91) * mm, v(2.6, 26.26) * mm, v(2.6, 24.87) * mm], "startDerivative": vector(13.83, -9.17) * mm, "endDerivative": vector(3.72, -14.8) * mm});
            skFitSpline(sketch, "E170", {"points": [v(7.33, 24.87) * mm, v(8.46, 25.26) * mm, v(7.9, 27.06) * mm, v(7.9, 28.06) * mm, v(7.06, 28.1) * mm, v(5.95, 28) * mm, v(5.42, 27.11) * mm], "startDerivative": vector(9.25, 0.85) * mm, "endDerivative": vector(-2.49, -7.07) * mm});
            skFitSpline(sketch, "E171", {"points": [v(8.15, 26.3) * mm, v(9.26, 26.16) * mm, v(10.5, 27.56) * mm, v(10.06, 28.56) * mm, v(10.1, 29.26) * mm, v(9.26, 29.76) * mm, v(8.46, 30.06) * mm, v(7.46, 29.7) * mm, v(6.76, 28.76) * mm, v(6.32, 28.1) * mm], "startDerivative": vector(8.92, -3.87) * mm, "endDerivative": vector(-4.58, -6.2) * mm});
            skFitSpline(sketch, "E172", {"points": [v(-13.8, 23.8) * mm, v(-12.93, 25.26) * mm, v(-14.03, 26.91) * mm, v(-14.56, 26.91) * mm, v(-14.73, 27.8) * mm, v(-16.27, 27.11) * mm, v(-16.85, 26.1) * mm], "startDerivative": vector(6.96, 6.62) * mm, "endDerivative": vector(-1.96, -6.05) * mm});
            skFitSpline(sketch, "E173", {"points": [v(-16.85, 25.43) * mm, v(-16.52, 25.25) * mm, v(-16.17, 24.33) * mm], "startDerivative": vector(0.93, -0.28) * mm, "endDerivative": vector(0.47, -1.8) * mm});
            skFitSpline(sketch, "E174", {"points": [v(-13.14, 25.98) * mm, v(-11.52, 26.55) * mm, v(-11.52, 28.47) * mm, v(-11.52, 29.5) * mm, v(-12.93, 29.38) * mm, v(-13.76, 29.63) * mm, v(-14.73, 27.8) * mm], "startDerivative": vector(11.52, 1.32) * mm, "endDerivative": vector(-4.72, -13.22) * mm});
            skFitSpline(sketch, "E175", {"points": [v(-11.42, 27.11) * mm, v(-9.87, 27.8) * mm, v(-9.87, 29.18) * mm, v(-10.89, 30.07) * mm, v(-11.05, 31.14) * mm, v(-13.27, 31.55) * mm, v(-13.76, 29.63) * mm], "startDerivative": vector(10.88, 2.35) * mm, "endDerivative": vector(0.53, -13.09) * mm});
            skLineSegment(sketch, "E176", {"start": v(4.04, -30.83) * mm, "end": v(4.04, -30.82) * mm});
            skLineSegment(sketch, "E177", {"start": v(-11.44, 31.44) * mm, "end": v(-10.43, 31.84) * mm});
            skLineSegment(sketch, "E178", {"start": v(-10.43, 31.84) * mm, "end": v(-9.62, 32.65) * mm});
            skLineSegment(sketch, "E179", {"start": v(-9.62, 32.65) * mm, "end": v(-8.93, 31.14) * mm});
            skLineSegment(sketch, "E180", {"start": v(-8.93, 31.14) * mm, "end": v(-7.6, 30.17) * mm});
            skLineSegment(sketch, "E181", {"start": v(-7.6, 30.17) * mm, "end": v(-8.2, 28.85) * mm});
            skLineSegment(sketch, "E182", {"start": v(-8.2, 28.85) * mm, "end": v(-9.66, 28.41) * mm});
            skPoint(sketch, "E183.5.internal.snap0", {"position": v(-9.27, 31.9) * mm});
            skFitSpline(sketch, "E183", {"points": [v(-9.27, 31.9) * mm, v(-8.97, 33.04) * mm, v(-7.65, 33.8) * mm, v(-7.3, 34.54) * mm, v(-6.15, 33.6) * mm, v(-6.06, 31.9) * mm, v(-6.88, 30.77) * mm, v(-7.6, 30.17) * mm], "startDerivative": vector(0.05, 9.48) * mm, "endDerivative": vector(-5.81, -4.4) * mm});
            skFitSpline(sketch, "E184", {"points": [v(-6.31, 31.42) * mm, v(-5.25, 30.73) * mm, v(-4.48, 31.24) * mm, v(-3.16, 31.24) * mm, v(-2.9, 33.04) * mm, v(-3.33, 34.5) * mm, v(-4.78, 34.2) * mm, v(-5.72, 35.05) * mm, v(-6.67, 34.24) * mm], "startDerivative": vector(9.51, -9.34) * mm, "endDerivative": vector(-8.3, -11.28) * mm});
            skFitSpline(sketch, "E185", {"points": [v(-3.02, 34.1) * mm, v(-2.34, 35.05) * mm, v(-0.42, 34.88) * mm, v(0.52, 34.5) * mm, v(0, 33.5) * mm, v(0.65, 32.44) * mm, v(-1.14, 31.76) * mm, v(-2.93, 31.57) * mm], "startDerivative": vector(3.8, 9.23) * mm, "endDerivative": vector(-9.74, -0.65) * mm});
            skFitSpline(sketch, "E186", {"points": [v(0, 32) * mm, v(0.6, 31.03) * mm, v(1.5, 31.33) * mm, v(1.6, 32.35) * mm, v(2.5, 33.55) * mm, v(1.68, 34.15) * mm, v(1.5, 35.1) * mm, v(0, 34.8) * mm], "startDerivative": vector(2.92, -8.97) * mm, "endDerivative": vector(-12.08, -4.77) * mm});
            skFitSpline(sketch, "E187", {"points": [v(7.88, 29.96) * mm, v(6.68, 30.17) * mm, v(6.51, 32.31) * mm, v(7.46, 32.1) * mm, v(8.13, 34.01) * mm, v(9.68, 32.78) * mm, v(11.18, 32.18) * mm, v(10.72, 30.44) * mm, v(10.1, 29.26) * mm], "startDerivative": vector(-12.44, -2.64) * mm, "endDerivative": vector(-4.85, -8.9) * mm});
            skFitSpline(sketch, "E188", {"points": [v(6.35, 31.16) * mm, v(4.5, 31.16) * mm, v(4.25, 32.1) * mm, v(3.13, 32.61) * mm, v(3.73, 34.01) * mm, v(3.99, 35.35) * mm, v(4.8, 34.88) * mm, v(5.74, 35.86) * mm, v(8.13, 34.01) * mm], "startDerivative": vector(-17.35, -3.37) * mm, "endDerivative": vector(15.34, -17.76) * mm});
            skFitSpline(sketch, "E189", {"points": [v(3.86, 32.31) * mm, v(3.4, 31.2) * mm, v(2.75, 31.63) * mm, v(1.5, 31.33) * mm], "startDerivative": vector(-1.13, -4.65) * mm, "endDerivative": vector(-3.69, -1.82) * mm});
            skFitSpline(sketch, "E190", {"points": [v(1.57, 34.7) * mm, v(2.53, 35.05) * mm, v(3, 34.4) * mm, v(3.99, 35.35) * mm], "startDerivative": vector(3.34, 2.23) * mm, "endDerivative": vector(2.97, 4.1) * mm});
            skFitSpline(sketch, "E191", {"points": [v(-3.93, -13.01) * mm, v(-0.7, -13.01) * mm, v(3.99, -13.01) * mm, v(6.98, -12.95) * mm], "startDerivative": vector(9.57, 0.01) * mm, "endDerivative": vector(9.1, 0.25) * mm});
            skFitSpline(sketch, "E192", {"points": [v(-4.09, -12.48) * mm, v(-2.92, -11.84) * mm, v(2.05, -11.59) * mm, v(6.68, -11.84) * mm], "startDerivative": vector(4.31, 3.46) * mm, "endDerivative": vector(11.2, -0.76) * mm});
            skFitSpline(sketch, "E193", {"points": [v(-2.33, -50.5) * mm, v(-1.97, -51.15) * mm], "startDerivative": vector(0.36, -0.65) * mm, "endDerivative": vector(0.36, -0.65) * mm});
            skLineSegment(sketch, "E194", {"start": v(-16.85, 26.1) * mm, "end": v(-16.85, 26.1) * mm});
            skLineSegment(sketch, "E195", {"start": v(18.89, -4.64) * mm, "end": v(18.88, -4.64) * mm});
            skSolve(sketch);
        }
        {
            var Q0;
            {var subQ24=sQuery(id+"F0.wireOp",EDGE,"E58");Q0=makeQuery(id+"F0.imprint","IMPRINT",FACE,{"disambiguationData":[TD([[makeQuery(id+"F0.imprint","IMPRINT",EDGE,{"derivedFrom":subQ24}),1.0]])]});}
            var Q1;
            {var subQ0=sQuery(id+"F0.wireOp",EDGE,"E168");Q1=makeQuery(id+"F0.imprint","IMPRINT",FACE,{"disambiguationData":[TD([[makeQuery(id+"F0.imprint","IMPRINT",EDGE,{"derivedFrom":subQ0}),-1.0]])]});}
            var Q2;
            Q2=makeQuery(id+"F0.imprint","IMPRINT",FACE,{"disambiguationData":[TD([[makeQuery(id+"F0.imprint","IMPRINT",EDGE,{"derivedFrom":sQuery(id+"F0.wireOp",EDGE,"E0")}),-1.0]])]});
            var Q3;
            Q3=makeQuery(id+"F0.imprint","IMPRINT",FACE,{"disambiguationData":[TD([[makeQuery(id+"F0.imprint","IMPRINT",EDGE,{"derivedFrom":sQuery(id+"F0.wireOp",EDGE,"E55")}),-1.0]])]});
            var Q4;
            Q4=makeQuery(id+"F0.imprint","IMPRINT",FACE,{"disambiguationData":[TD([[makeQuery(id+"F0.imprint","IMPRINT",EDGE,{"derivedFrom":sQuery(id+"F0.wireOp",EDGE,"E100")}),-1.0]])]});
            var Q5;
            Q5=makeQuery(id+"F0.imprint","IMPRINT",FACE,{"disambiguationData":[TD([[makeQuery(id+"F0.imprint","IMPRINT",EDGE,{"derivedFrom":sQuery(id+"F0.wireOp",EDGE,"E90")}),-1.0]])]});
            var Q6;
            Q6=makeQuery(id+"F0.imprint","IMPRINT",FACE,{"disambiguationData":[TD([[makeQuery(id+"F0.imprint","IMPRINT",EDGE,{"derivedFrom":sQuery(id+"F0.wireOp",EDGE,"E95")}),1.0]])]});
            var Q7;
            Q7=makeQuery(id+"F0.imprint","IMPRINT",FACE,{"disambiguationData":[TD([[makeQuery(id+"F0.imprint","IMPRINT",EDGE,{"derivedFrom":sQuery(id+"F0.wireOp",EDGE,"E46")}),1.0]])]});
            var Q8;
            {var subQ3=sQuery(id+"F0.wireOp",EDGE,"E57");Q8=makeQuery(id+"F0.imprint","IMPRINT",FACE,{"disambiguationData":[TD([[makeQuery(id+"F0.imprint","IMPRINT",EDGE,{"derivedFrom":subQ3}),1.0]])]});}
            var Q9;
            {var subQ3=sQuery(id+"F0.wireOp",EDGE,"E111");Q9=makeQuery(id+"F0.imprint","IMPRINT",FACE,{"disambiguationData":[TD([[makeQuery(id+"F0.imprint","IMPRINT",EDGE,{"derivedFrom":subQ3}),-1.0]])]});}
            var Q10;
            Q10=makeQuery(id+"F0.imprint","IMPRINT",FACE,{"disambiguationData":[TD([[makeQuery(id+"F0.imprint","IMPRINT",EDGE,{"derivedFrom":sQuery(id+"F0.wireOp",EDGE,"E56")}),1.0]])]});
            var Q11;
            {var subQ4=sQuery(id+"F0.wireOp",EDGE,"E107");Q11=makeQuery(id+"F0.imprint","IMPRINT",FACE,{"disambiguationData":[TD([[makeQuery(id+"F0.imprint","IMPRINT",EDGE,{"derivedFrom":subQ4}),1.0]])]});}
            var Q12;
            {var subQ1=sQuery(id+"F0.wireOp",EDGE,"E122");Q12=makeQuery(id+"F0.imprint","IMPRINT",FACE,{"disambiguationData":[TD([[makeQuery(id+"F0.imprint","IMPRINT",EDGE,{"derivedFrom":subQ1}),-1.0]])]});}
            var Q13;
            {var subQ1=sQuery(id+"F0.wireOp",EDGE,"E139");Q13=makeQuery(id+"F0.imprint","IMPRINT",FACE,{"disambiguationData":[TD([[makeQuery(id+"F0.imprint","IMPRINT",EDGE,{"derivedFrom":subQ1}),-1.0]])]});}
            var Q14;
            {var subQ2=sQuery(id+"F0.wireOp",EDGE,"E138");Q14=makeQuery(id+"F0.imprint","IMPRINT",FACE,{"disambiguationData":[TD([[makeQuery(id+"F0.imprint","IMPRINT",EDGE,{"derivedFrom":subQ2}),-1.0]])]});}
            var Q15;
            {var subQ1=sQuery(id+"F0.wireOp",EDGE,"E137");Q15=makeQuery(id+"F0.imprint","IMPRINT",FACE,{"disambiguationData":[TD([[makeQuery(id+"F0.imprint","IMPRINT",EDGE,{"derivedFrom":subQ1}),-1.0]])]});}
            var Q16;
            {var subQ3=sQuery(id+"F0.wireOp",EDGE,"E153");Q16=makeQuery(id+"F0.imprint","IMPRINT",FACE,{"disambiguationData":[TD([[makeQuery(id+"F0.imprint","IMPRINT",EDGE,{"derivedFrom":subQ3}),-1.0]])]});}
            extrude(context, id + "F1", {"entities" : qUnion([Q0, Q1, Q2, Q3, Q4, Q5, Q6, Q7, Q8, Q9, Q10, Q11, Q12, Q13, Q14, Q15, Q16]), "depth" : 9.14 * mm});
        }
    });
